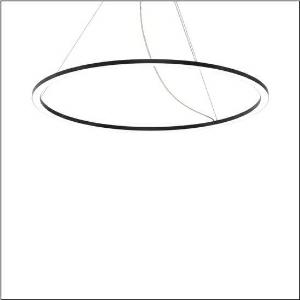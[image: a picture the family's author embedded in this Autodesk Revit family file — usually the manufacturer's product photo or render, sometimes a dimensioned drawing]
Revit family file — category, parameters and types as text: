
# Revit family: silica_21_ring-d_5pjbd4d1104a
name_source: partatom
category: Lighting Fixtures
units: mm (PartAtom-declared; Revit-internal decimal feet)

## family parameters
Cut with Voids When Loaded = No
Host = Face
Light Source = No
Part Type = Normal
Room Calculation Point = No
Round Connector Dimension = Use Diameter
Shared = No

## types (1)
- Silica 21 Ring-D (1 x LED, 10840 lm, 125 W, 3000K)
    Apparent Load = 125 VA
    CIE Flux Codes = 37 69 92 100 100
    Color Rendering = 80
    Color Temperature = 3000K
    Default Elevation = 1800 mm
    Description = Silica 21 Ring-D, suspended luminaire, of PMMA, frosted, light emission: ring underside luminous distribution, primary light characteristic: symmetric, installation type: suspended mounting, LED, rated luminous flux: 10.840lm, luminous efficacy: 87lm/W, light colour: 830, colour temperature: 3000K, control gear: DALI 2, with terminal, 5-pole, mains connection: 230V, AC/DC, 0/50..60Hz, rated input power: 125W, housing, of extruded aluminium section, jet black (RAL 9005), diameter: 1.450mm, ceiling canopy, jet black (RAL 9005), protection rating (lamp compartment): IP40, insulation class (complete): insulation class I (protective earthing), certification: CE, impact resistance: IK02, permissible operating ambient temperature: 0..+35°C, packaging unit: 1 piece
    Height = 25 mm  [stored 0.082021 ft]
    Lamp = 1 x LED
    Lamp Light Flux = 10840 lm
    Lamp Power = 125 W
    Lamp count = 1
    Length = 1450 mm
    Luminous efficacy = 87 lm/W
    Manufacturer = Siteco
    ModVariant = No
    Model = 5PJBD4D1104A
    Mounting Place = Ceiling
    Mounting Type = Pendant
    Number of Poles = 1
    OnlyDefault = Yes
    Power Factor = 1
    Product Name = Silica 21 Ring-D
    Product group = suspended luminaire
    ProductGroupID = 904
    Protection Class = Protection class I
    Protection Degree = IP 40
    RLX_Detail_Level = 1
    RLX_Emergency_Light_Flux = 0 lm
    RLX_Emergency_Type = 0
    RLX_Emergency_Type_DB = No
    RlxData = <blob elided: 19381 chars, md5=129f15a7>
    Socket = socket
    Standby Power = 0 W
    System Light Flux = 10840 lm
    System Power = 125 W
    Type Comments = Product without accessories
    Type Image = l_1258357.jpg
    URL = http://relux.com
    VarID = ---
    Voltage = 0 V
    Weight = 0.00 kg
    Width = 0 mm  [stored 0 ft]

note: [stored X ft] marks values corroborated as IEEE doubles in the binary element streams (Revit-internal decimal feet)

## geometry (parser evidence)
native form markers: Blend x4, Sweep x9
no freeform markers — native parametric forms only
